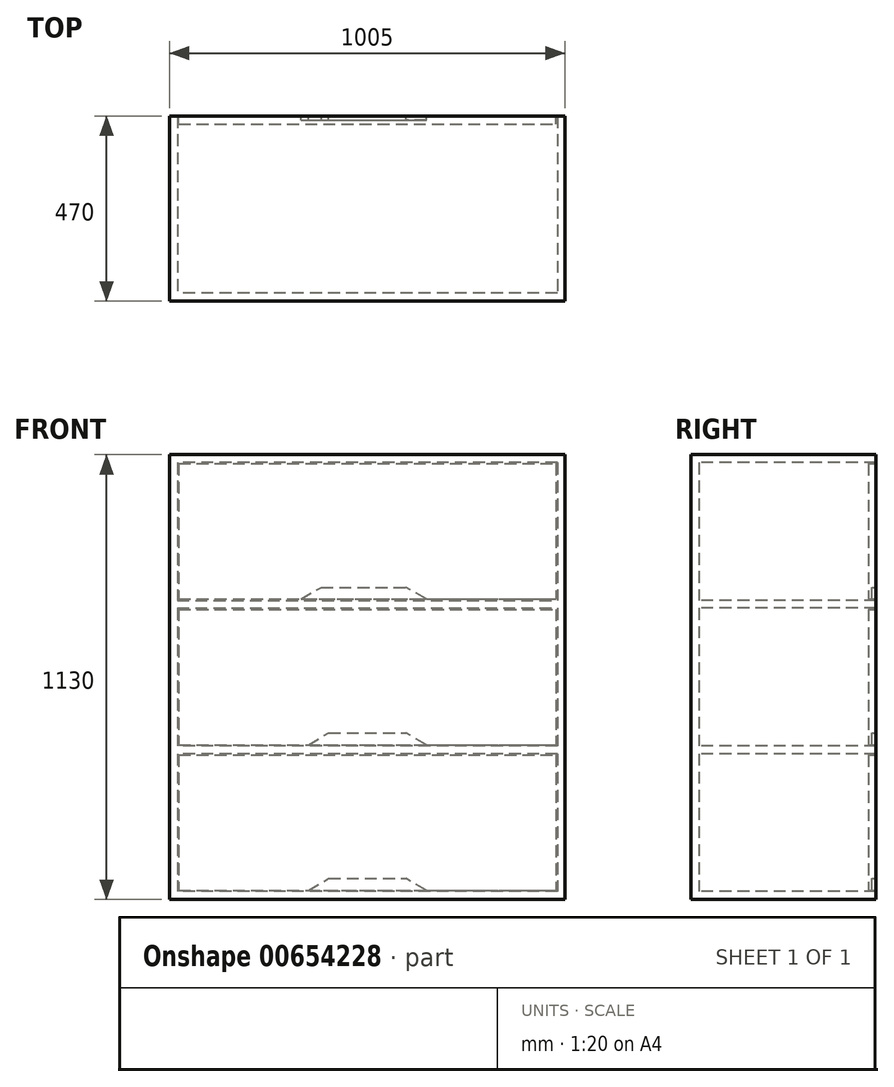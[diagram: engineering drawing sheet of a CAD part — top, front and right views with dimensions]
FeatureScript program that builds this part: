
annotation { "Feature Type Name" : "Feature", "Feature Type Description" : "" }
export const myFeature = defineFeature(function(context is Context, id is Id, definition is map)
    precondition{}
    {
        {
            var Q0;
            Q0=qCreatedBy(makeId("Top.planeOp"),FACE);
            var sketch = newSketch(context, id + "F0", { "sketchPlane" : qUnion([Q0])});
            skLineSegment(sketch, "E0.bottom", {"start": v(502.5, 275) * mm, "end": v(-502.5, 275) * mm});
            skLineSegment(sketch, "E0.top", {"start": v(502.5, -275) * mm, "end": v(-502.5, -275) * mm});
            skLineSegment(sketch, "E0.left", {"start": v(502.5, 275) * mm, "end": v(502.5, -275) * mm});
            skLineSegment(sketch, "E0.right", {"start": v(-502.5, 275) * mm, "end": v(-502.5, -275) * mm});
            skPoint(sketch, "E0.middle", {"position": v(0, 0) * mm});
            skSolve(sketch);
        }
        {
            var Q0;
            Q0=makeQuery(id+"F0.imprint","IMPRINT",FACE,{"disambiguationData":[TD([[makeQuery(id+"F0.imprint","IMPRINT",EDGE,{"derivedFrom":sQuery(id+"F0.wireOp",EDGE,"E0.bottom")}),1.0]])]});
            extrude(context, id + "F1", {"entities" : qUnion([Q0]), "depth" : 20 * mm, "offsetDistance" : 25.4 * mm});
        }
        {
            var Q0;
            Q0=makeQuery(id+"F1.opExtrude","CAP_FACE",FACE,{"disambiguationData":[OSD([sQuery(id+"F0.wireOp",EDGE,"E0.bottom"),sQuery(id+"F0.wireOp",EDGE,"E0.top"),sQuery(id+"F0.wireOp",EDGE,"E0.left"),sQuery(id+"F0.wireOp",EDGE,"E0.right")])],"isStart":false});
            var sketch = newSketch(context, id + "F2", { "sketchPlane" : qUnion([Q0])});
            skLineSegment(sketch, "E1.bottom", {"start": v(-502.5, 275) * mm, "end": v(502.5, 275) * mm});
            skLineSegment(sketch, "E1.top", {"start": v(-502.5, 255) * mm, "end": v(502.5, 255) * mm});
            skLineSegment(sketch, "E1.left", {"start": v(-502.5, 275) * mm, "end": v(-502.5, 255) * mm});
            skLineSegment(sketch, "E1.right", {"start": v(502.5, 275) * mm, "end": v(502.5, 255) * mm});
            skSolve(sketch);
        }
        {
            var Q0;
            Q0 = qSketchRegion(id + "F2", true);
            extrude(context, id + "F3", {"entities" : qUnion([Q0]), "operationType" : NewBodyOperationType.ADD, "depth" : 2200 * mm, "offsetDistance" : 25.4 * mm});
        }
        {
            var Q0;
            Q0=makeQuery(id+"F1.opExtrude","CAP_FACE",FACE,{"disambiguationData":[OSD([sQuery(id+"F0.wireOp",EDGE,"E0.bottom"),sQuery(id+"F0.wireOp",EDGE,"E0.top"),sQuery(id+"F0.wireOp",EDGE,"E0.left"),sQuery(id+"F0.wireOp",EDGE,"E0.right")])],"isStart":false});
            var sketch = newSketch(context, id + "F4", { "sketchPlane" : qUnion([Q0])});
            skLineSegment(sketch, "E2.bottom", {"start": v(-502.5, 255) * mm, "end": v(-482.5, 255) * mm});
            skLineSegment(sketch, "E2.top", {"start": v(-502.5, -275) * mm, "end": v(-482.5, -275) * mm});
            skLineSegment(sketch, "E2.left", {"start": v(-502.5, 255) * mm, "end": v(-502.5, -275) * mm});
            skLineSegment(sketch, "E2.right", {"start": v(-482.5, 255) * mm, "end": v(-482.5, -275) * mm});
            skLineSegment(sketch, "E3.bottom", {"start": v(502.5, 255) * mm, "end": v(482.5, 255) * mm});
            skLineSegment(sketch, "E3.top", {"start": v(502.5, -275) * mm, "end": v(482.5, -275) * mm});
            skLineSegment(sketch, "E3.left", {"start": v(502.5, 255) * mm, "end": v(502.5, -275) * mm});
            skLineSegment(sketch, "E3.right", {"start": v(482.5, 255) * mm, "end": v(482.5, -275) * mm});
            skSolve(sketch);
        }
        {
            var Q0;
            Q0 = qSketchRegion(id + "F4", true);
            extrude(context, id + "F5", {"entities" : qUnion([Q0]), "operationType" : NewBodyOperationType.ADD, "depth" : 2200 * mm, "offsetDistance" : 25.4 * mm});
        }
        {
            var Q0;
            Q0=makeQuery(id+"F5.boolean.opBoolean","MERGE",FACE,{"derivedFrom":[makeQuery(id+"F3.opExtrude","CAP_FACE",FACE,{"disambiguationData":[OSD([sQuery(id+"F2.wireOp",EDGE,"E1.bottom"),sQuery(id+"F2.wireOp",EDGE,"E1.top"),sQuery(id+"F2.wireOp",EDGE,"E1.left"),sQuery(id+"F2.wireOp",EDGE,"E1.right")])],"isStart":false}),makeQuery(id+"F5.opExtrude","CAP_FACE",FACE,{"disambiguationData":[OSD([sQuery(id+"F4.wireOp",EDGE,"E2.bottom"),sQuery(id+"F4.wireOp",EDGE,"E2.top"),sQuery(id+"F4.wireOp",EDGE,"E2.left"),sQuery(id+"F4.wireOp",EDGE,"E2.right")])],"isStart":false}),makeQuery(id+"F5.opExtrude","CAP_FACE",FACE,{"disambiguationData":[OSD([sQuery(id+"F4.wireOp",EDGE,"E3.bottom"),sQuery(id+"F4.wireOp",EDGE,"E3.top"),sQuery(id+"F4.wireOp",EDGE,"E3.left"),sQuery(id+"F4.wireOp",EDGE,"E3.right")])],"isStart":false})]});
            var sketch = newSketch(context, id + "F6", { "sketchPlane" : qUnion([Q0])});
            skLineSegment(sketch, "E4.bottom", {"start": v(-502.5, 275) * mm, "end": v(502.5, 275) * mm});
            skLineSegment(sketch, "E4.top", {"start": v(-502.5, -275) * mm, "end": v(502.5, -275) * mm});
            skLineSegment(sketch, "E4.left", {"start": v(-502.5, 275) * mm, "end": v(-502.5, -275) * mm});
            skLineSegment(sketch, "E4.right", {"start": v(502.5, 275) * mm, "end": v(502.5, -275) * mm});
            skSolve(sketch);
        }
        {
            var Q0;
            Q0 = qSketchRegion(id + "F6", true);
            extrude(context, id + "F7", {"entities" : qUnion([Q0]), "operationType" : NewBodyOperationType.ADD, "oppositeDirection" : true, "depth" : 20 * mm, "offsetDistance" : 25.4 * mm});
        }
        {
            var Q0;
            {var subQ1=sQuery(id+"FTxYvzd5MEbboGn_1.wireOp",EDGE,"0aFY1y2h-sFPR-yNvK-VnQl-ctgHC5mLAOd9.top");Q0=makeQuery(id+"FLdDUuKQBrVvMx0_1.boolean.opBoolean","SPLIT",FACE,{"disambiguationData":[TD([makeQuery(id+"FLdDUuKQBrVvMx0_1.opExtrude","SWEPT_FACE",FACE,{"disambiguationData":[OSD([subQ1])]})])],"derivedFrom":makeQuery(id+"F5.opExtrude","SWEPT_FACE",FACE,{"disambiguationData":[OSD([sQuery(id+"F4.wireOp",EDGE,"E3.right")])]})});}
            var sketch = newSketch(context, id + "F8", { "sketchPlane" : qUnion([Q0])});
            skCircle(sketch, "E5", {"center": v(0, 1643.23) * mm, "radius": 17.76 * mm});
            skSolve(sketch);
        }
        {
            var Q0;
            Q0 = qSketchRegion(id + "F8", true);
            extrude(context, id + "F9", {"entities" : qUnion([Q0]), "operationType" : NewBodyOperationType.ADD, "depth" : 982.98 * mm, "offsetDistance" : 25.4 * mm});
        }
        {
            var Q0;
            Q0=makeQuery(id+"F3.boolean.opBoolean","MERGE",FACE,{"derivedFrom":[makeQuery(id+"F1.opExtrude","SWEPT_FACE",FACE,{"disambiguationData":[OSD([sQuery(id+"F0.wireOp",EDGE,"E0.bottom")])]}),makeQuery(id+"F3.opExtrude","SWEPT_FACE",FACE,{"disambiguationData":[OSD([sQuery(id+"F2.wireOp",EDGE,"E1.bottom")])]})]});
            var sketch = newSketch(context, id + "F10", { "sketchPlane" : qUnion([Q0])});
            skLineSegment(sketch, "E6.bottom", {"start": v(-502.5, 0) * mm, "end": v(502.5, 0) * mm});
            skLineSegment(sketch, "E6.top", {"start": v(-502.5, 1130) * mm, "end": v(502.5, 1130) * mm});
            skLineSegment(sketch, "E6.left", {"start": v(-502.5, 0) * mm, "end": v(-502.5, 1130) * mm});
            skLineSegment(sketch, "E6.right", {"start": v(502.5, 0) * mm, "end": v(502.5, 1130) * mm});
            skSolve(sketch);
        }
        {
            var Q0;
            Q0 = qSketchRegion(id + "F10", true);
            extrude(context, id + "F11", {"entities" : qUnion([Q0]), "depth" : 20 * mm, "offsetDistance" : 25 * mm});
        }
        {
            var Q0;
            Q0=makeQuery(id+"F11.opExtrude","CAP_FACE",FACE,{"disambiguationData":[OSD([sQuery(id+"F10.wireOp",EDGE,"E6.bottom"),sQuery(id+"F10.wireOp",EDGE,"E6.top"),sQuery(id+"F10.wireOp",EDGE,"E6.left"),sQuery(id+"F10.wireOp",EDGE,"E6.right")])],"isStart":false});
            var sketch = newSketch(context, id + "F12", { "sketchPlane" : qUnion([Q0])});
            skLineSegment(sketch, "E7.bottom", {"start": v(-502.5, 1130) * mm, "end": v(502.5, 1130) * mm});
            skLineSegment(sketch, "E7.top", {"start": v(-482.5, 1110) * mm, "end": v(482.5, 1110) * mm});
            skLineSegment(sketch, "E7.left", {"start": v(-502.5, 1130) * mm, "end": v(-502.5, 1110) * mm});
            skLineSegment(sketch, "E7.right", {"start": v(502.5, 1130) * mm, "end": v(502.5, 1110) * mm});
            skLineSegment(sketch, "E8.bottom", {"start": v(482.5, 740) * mm, "end": v(-482.5, 740) * mm});
            skLineSegment(sketch, "E8.top", {"start": v(482.5, 760) * mm, "end": v(-482.5, 760) * mm});
            skLineSegment(sketch, "E8.left", {"start": v(502.5, 740) * mm, "end": v(502.5, 760) * mm});
            skLineSegment(sketch, "E8.right", {"start": v(-502.5, 740) * mm, "end": v(-502.5, 760) * mm});
            skLineSegment(sketch, "E9", {"start": v(-502.5, 740) * mm, "end": v(-502.5, 390) * mm});
            skLineSegment(sketch, "E10.bottom", {"start": v(-482.5, 390) * mm, "end": v(482.5, 390) * mm});
            skLineSegment(sketch, "E10.top", {"start": v(-482.5, 370) * mm, "end": v(482.5, 370) * mm});
            skLineSegment(sketch, "E10.left", {"start": v(-502.5, 390) * mm, "end": v(-502.5, 370) * mm});
            skLineSegment(sketch, "E10.right", {"start": v(502.5, 390) * mm, "end": v(502.5, 370) * mm});
            skLineSegment(sketch, "E11.bottom", {"start": v(-502.5, 0) * mm, "end": v(502.5, 0) * mm});
            skLineSegment(sketch, "E11.top", {"start": v(-482.5, 20) * mm, "end": v(482.5, 20) * mm});
            skLineSegment(sketch, "E11.left", {"start": v(-502.5, 0) * mm, "end": v(-502.5, 20) * mm});
            skLineSegment(sketch, "E11.right", {"start": v(502.5, 0) * mm, "end": v(502.5, 20) * mm});
            skLineSegment(sketch, "E12", {"start": v(-502.5, 1110) * mm, "end": v(-502.5, 0) * mm});
            skLineSegment(sketch, "E13", {"start": v(502.5, 1110) * mm, "end": v(502.5, 20) * mm});
            skLineSegment(sketch, "E14.left", {"start": v(-502.5, 1110) * mm, "end": v(-502.5, 20) * mm});
            skLineSegment(sketch, "E14.right", {"start": v(-482.5, 1110) * mm, "end": v(-482.5, 760) * mm});
            skLineSegment(sketch, "E15.top", {"start": v(502.5, 0) * mm, "end": v(482.5, 0) * mm});
            skLineSegment(sketch, "E15.left", {"start": v(502.5, 1110) * mm, "end": v(502.5, 0) * mm});
            skLineSegment(sketch, "E15.right", {"start": v(482.5, 1110) * mm, "end": v(482.5, 760) * mm});
            skLineSegment(sketch, "E16.trimOffspring", {"start": v(-482.5, 740) * mm, "end": v(-482.5, 390) * mm});
            skLineSegment(sketch, "E17.trimOffspring", {"start": v(482.5, 740) * mm, "end": v(482.5, 390) * mm});
            skLineSegment(sketch, "E18.trimOffspring", {"start": v(482.5, 370) * mm, "end": v(482.5, 20) * mm});
            skLineSegment(sketch, "E19.trimOffspring", {"start": v(-482.5, 370) * mm, "end": v(-482.5, 20) * mm});
            skSolve(sketch);
        }
        {
            var Q0;
            Q0 = qSketchRegion(id + "F12", true);
            extrude(context, id + "F13", {"entities" : qUnion([Q0]), "operationType" : NewBodyOperationType.ADD, "depth" : 450 * mm, "offsetDistance" : 25 * mm});
        }
        {
            var Q0;
            Q0=makeQuery(id+"F13.opExtrude","CAP_FACE",FACE,{"disambiguationData":[OSD([sQuery(id+"F12.wireOp",EDGE,"E7.bottom"),sQuery(id+"F12.wireOp",EDGE,"E7.top"),sQuery(id+"F12.wireOp",EDGE,"E7.left"),sQuery(id+"F12.wireOp",EDGE,"E7.right"),sQuery(id+"F12.wireOp",EDGE,"E8.bottom"),sQuery(id+"F12.wireOp",EDGE,"E8.top"),sQuery(id+"F12.wireOp",EDGE,"E8.left"),sQuery(id+"F12.wireOp",EDGE,"E8.right"),sQuery(id+"F12.wireOp",EDGE,"E9"),sQuery(id+"F12.wireOp",EDGE,"E10.bottom"),sQuery(id+"F12.wireOp",EDGE,"E10.top"),sQuery(id+"F12.wireOp",EDGE,"E10.left"),sQuery(id+"F12.wireOp",EDGE,"E10.right"),sQuery(id+"F12.wireOp",EDGE,"E11.bottom"),sQuery(id+"F12.wireOp",EDGE,"E11.top"),sQuery(id+"F12.wireOp",EDGE,"E11.left"),sQuery(id+"F12.wireOp",EDGE,"E11.right"),sQuery(id+"F12.wireOp",EDGE,"E12"),sQuery(id+"F12.wireOp",EDGE,"E13"),sQuery(id+"F12.wireOp",EDGE,"E14.right"),sQuery(id+"F12.wireOp",EDGE,"E15.right"),sQuery(id+"F12.wireOp",EDGE,"E16.trimOffspring"),sQuery(id+"F12.wireOp",EDGE,"E17.trimOffspring"),sQuery(id+"F12.wireOp",EDGE,"E18.trimOffspring"),sQuery(id+"F12.wireOp",EDGE,"E19.trimOffspring")])],"isStart":false});
            var sketch = newSketch(context, id + "F14", { "sketchPlane" : qUnion([Q0])});
            skLineSegment(sketch, "E20", {"start": v(0, 1110) * mm, "end": v(0, 760) * mm});
            skLineSegment(sketch, "E21", {"start": v(0, 740) * mm, "end": v(0, 390) * mm});
            skLineSegment(sketch, "E22", {"start": v(0, 370) * mm, "end": v(0, 20) * mm});
            skLineSegment(sketch, "E23.bottom", {"start": v(479.5, 1107) * mm, "end": v(-479.5, 1107) * mm});
            skLineSegment(sketch, "E23.top", {"start": v(479.5, 763) * mm, "end": v(-479.5, 763) * mm});
            skLineSegment(sketch, "E23.left", {"start": v(479.5, 1107) * mm, "end": v(479.5, 763) * mm});
            skLineSegment(sketch, "E23.right", {"start": v(-479.5, 1107) * mm, "end": v(-479.5, 763) * mm});
            skPoint(sketch, "E23.middle", {"position": v(0, 935) * mm});
            skLineSegment(sketch, "E24.bottom", {"start": v(479.5, 737) * mm, "end": v(-479.5, 737) * mm});
            skLineSegment(sketch, "E24.top", {"start": v(479.5, 393) * mm, "end": v(-479.5, 393) * mm});
            skLineSegment(sketch, "E24.left", {"start": v(479.5, 737) * mm, "end": v(479.5, 393) * mm});
            skLineSegment(sketch, "E24.right", {"start": v(-479.5, 737) * mm, "end": v(-479.5, 393) * mm});
            skPoint(sketch, "E24.middle", {"position": v(0, 565) * mm});
            skLineSegment(sketch, "E25.bottom", {"start": v(479.5, 367) * mm, "end": v(-479.5, 367) * mm});
            skLineSegment(sketch, "E25.top", {"start": v(479.5, 23) * mm, "end": v(-479.5, 23) * mm});
            skLineSegment(sketch, "E25.left", {"start": v(479.5, 367) * mm, "end": v(479.5, 23) * mm});
            skLineSegment(sketch, "E25.right", {"start": v(-479.5, 367) * mm, "end": v(-479.5, 23) * mm});
            skPoint(sketch, "E25.middle", {"position": v(0, 195) * mm});
            skSolve(sketch);
        }
        {
            var Q0;
            Q0 = qSketchRegion(id + "F14", true);
            extrude(context, id + "F15", {"entities" : qUnion([Q0]), "oppositeDirection" : true, "depth" : 20 * mm, "offsetDistance" : 25 * mm});
        }
        {
            var Q0;
            Q0=makeQuery(id+"F15.opExtrude","CAP_FACE",FACE,{"disambiguationData":[OSD([sQuery(id+"F14.wireOp",EDGE,"E23.bottom"),sQuery(id+"F14.wireOp",EDGE,"E23.top"),sQuery(id+"F14.wireOp",EDGE,"E23.left"),sQuery(id+"F14.wireOp",EDGE,"E23.right")])],"isStart":true});
            var sketch = newSketch(context, id + "F16", { "sketchPlane" : qUnion([Q0])});
            skLineSegment(sketch, "E26.bottom", {"start": v(168.8, 763) * mm, "end": v(-150, 763) * mm});
            skLineSegment(sketch, "E26.top", {"start": v(116.83, 793) * mm, "end": v(-98.04, 793) * mm});
            skPoint(sketch, "E26.middle", {"position": v(78.8, 778) * mm});
            skLineSegment(sketch, "E27", {"start": v(-150, 763) * mm, "end": v(-98.04, 793) * mm});
            skLineSegment(sketch, "E28", {"start": v(168.8, 763) * mm, "end": v(116.83, 793) * mm});
            skPoint(sketch, "E26.right.end.orphan", {"position": v(-11.2, 793) * mm});
            skPoint(sketch, "E29.orphan", {"position": v(157.6, 793) * mm});
            skPoint(sketch, "E30.start.orphan", {"position": v(0, 763) * mm});
            skPoint(sketch, "E26.left.end.orphan", {"position": v(307.6, 793) * mm});
            skSolve(sketch);
        }
        {
            var Q0;
            Q0 = qSketchRegion(id + "F16", true);
            extrude(context, id + "F17", {"entities" : qUnion([Q0]), "operationType" : NewBodyOperationType.REMOVE, "oppositeDirection" : true, "depth" : 10 * mm, "offsetDistance" : 25 * mm});
        }
        {
            var Q0;
            Q0=makeQuery(id+"F15.opExtrude","CAP_FACE",FACE,{"disambiguationData":[OSD([sQuery(id+"F14.wireOp",EDGE,"E24.bottom"),sQuery(id+"F14.wireOp",EDGE,"E24.top"),sQuery(id+"F14.wireOp",EDGE,"E24.left"),sQuery(id+"F14.wireOp",EDGE,"E24.right")])],"isStart":true});
            var sketch = newSketch(context, id + "F18", { "sketchPlane" : qUnion([Q0])});
            skLineSegment(sketch, "E31", {"start": v(0, 393) * mm, "end": v(0, 423) * mm});
            skLineSegment(sketch, "E32.bottom", {"start": v(150, 393) * mm, "end": v(-150, 393) * mm});
            skLineSegment(sketch, "E32.top", {"start": v(98.04, 423) * mm, "end": v(-98.04, 423) * mm});
            skPoint(sketch, "E32.middle", {"position": v(0, 408) * mm});
            skLineSegment(sketch, "E33", {"start": v(-150, 393) * mm, "end": v(-98.04, 423) * mm});
            skLineSegment(sketch, "E34", {"start": v(150, 393) * mm, "end": v(98.04, 423) * mm});
            skPoint(sketch, "E35.orphan", {"position": v(-150, 423) * mm});
            skPoint(sketch, "E32.left.end.orphan", {"position": v(150, 423) * mm});
            skSolve(sketch);
        }
        {
            var Q0;
            Q0 = qSketchRegion(id + "F18", true);
            extrude(context, id + "F19", {"entities" : qUnion([Q0]), "operationType" : NewBodyOperationType.REMOVE, "oppositeDirection" : true, "depth" : 10 * mm, "offsetDistance" : 25 * mm});
        }
        {
            var Q0;
            Q0=makeQuery(id+"F15.opExtrude","CAP_FACE",FACE,{"disambiguationData":[OSD([sQuery(id+"F14.wireOp",EDGE,"E25.bottom"),sQuery(id+"F14.wireOp",EDGE,"E25.top"),sQuery(id+"F14.wireOp",EDGE,"E25.left"),sQuery(id+"F14.wireOp",EDGE,"E25.right")])],"isStart":true});
            var sketch = newSketch(context, id + "F20", { "sketchPlane" : qUnion([Q0])});
            skLineSegment(sketch, "E36", {"start": v(0, 23) * mm, "end": v(0, 53) * mm});
            skLineSegment(sketch, "E37.bottom", {"start": v(150, 23) * mm, "end": v(-150, 23) * mm});
            skLineSegment(sketch, "E37.top", {"start": v(98.04, 53) * mm, "end": v(-98.04, 53) * mm});
            skPoint(sketch, "E37.middle", {"position": v(0, 38) * mm});
            skLineSegment(sketch, "E38", {"start": v(-150, 23) * mm, "end": v(-98.04, 53) * mm});
            skLineSegment(sketch, "E39", {"start": v(150, 23) * mm, "end": v(98.04, 53) * mm});
            skPoint(sketch, "E37.right.end.orphan", {"position": v(-150, 53) * mm});
            skPoint(sketch, "E37.left.end.orphan", {"position": v(150, 53) * mm});
            skSolve(sketch);
        }
        {
            var Q0;
            Q0 = qSketchRegion(id + "F20", true);
            extrude(context, id + "F21", {"entities" : qUnion([Q0]), "operationType" : NewBodyOperationType.REMOVE, "oppositeDirection" : true, "depth" : 10 * mm, "offsetDistance" : 25 * mm});
        }
        {
            var Q0;
            Q0=makeQuery(id+"F7.boolean.opBoolean","MERGE",FACE,{"derivedFrom":[makeQuery(id+"F5.boolean.opBoolean","MERGE",FACE,{"derivedFrom":[makeQuery(id+"F1.opExtrude","SWEPT_FACE",FACE,{"disambiguationData":[OSD([sQuery(id+"F0.wireOp",EDGE,"E0.top")])]}),makeQuery(id+"F5.opExtrude","SWEPT_FACE",FACE,{"disambiguationData":[OSD([sQuery(id+"F4.wireOp",EDGE,"E2.top")])]}),makeQuery(id+"F5.opExtrude","SWEPT_FACE",FACE,{"disambiguationData":[OSD([sQuery(id+"F4.wireOp",EDGE,"E3.top")])]})]}),makeQuery(id+"F7.opExtrude","SWEPT_FACE",FACE,{"disambiguationData":[OSD([sQuery(id+"F6.wireOp",EDGE,"E4.top")])]})]});
            var sketch = newSketch(context, id + "F22", { "sketchPlane" : qUnion([Q0])});
            skLineSegment(sketch, "E40", {"start": v(-502.5, 2220) * mm, "end": v(502.5, 2220) * mm});
            skLineSegment(sketch, "E41", {"start": v(502.5, 2220) * mm, "end": v(502.5, 0) * mm});
            skLineSegment(sketch, "E42", {"start": v(-502.5, 2220) * mm, "end": v(-502.5, 0) * mm});
            skLineSegment(sketch, "E43", {"start": v(-502.5, 0) * mm, "end": v(502.5, 0) * mm});
            skSolve(sketch);
        }
        {
            var Q0;
            Q0 = qSketchRegion(id + "F22", true);
            extrude(context, id + "F23", {"entities" : qUnion([Q0]), "operationType" : NewBodyOperationType.REMOVE, "oppositeDirection" : true, "depth" : 550 * mm, "offsetDistance" : 25 * mm});
        }
    });
